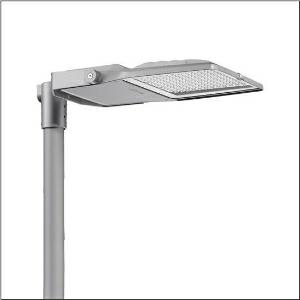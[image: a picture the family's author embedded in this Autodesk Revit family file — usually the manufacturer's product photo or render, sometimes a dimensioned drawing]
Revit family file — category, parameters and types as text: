
# Revit family: floodlight_fl_21_midi___pl64_5xa7782e2e3a_2f92
name_source: partatom
category: Lighting Fixtures
units: mm (PartAtom-declared; Revit-internal decimal feet)

## family parameters
Cut with Voids When Loaded = No
Host = Face
Light Source = No
Part Type = Normal
Room Calculation Point = No
Round Connector Dimension = Use Diameter
Shared = No

## types (1)
- --- (1 x LED, 25930 lm, 208.1 W, 3000K)
    Apparent Load = 208 VA
    CIE Flux Codes = 28 80 98 100 100
    Color Rendering = 70
    Color Temperature = 3000K
    Default Elevation = 1800 mm
    Description = Floodlight FL 21 midi, floodlight, primary light control with lens, of PMMA, primary optical cover: protective disc, of toughened safety glass, transparent, light distribution: PL64, light emission: direct distribution, installation type: surface-mounted, LED, High Power LED, rated luminous flux: 25.930lm, luminous efficacy: 124lm/W, light colour: 730, colour temperature: 3000K, control gear: ECG iQ, control: optimised constant luminous flux control (CLO 2.0), Desk-Remote (wireless, voltage-free reading and setting of iQ features in the workshop via application-optimized NFC function/RFID function), Smart-Wire, Night-Set, Temp-Guard, Auto-Match, Street-Remote, with terminal, 6-pole, mains connection: 220..240V, AC, 50/60Hz, start of lifetime: 208W, end of lifetime: 227W, reduction: 90W, luminaire housing, of diecast aluminium, powder-coated, Siteco® metallic grey (DB 702S), corrosivity category C5 according to DIN EN ISO 12944, mast bracket, of steel, galvanised, powder-coated, Siteco® metallic grey (DB 702S), protection rating (complete): IP66, insulation class (complete): insulation class II (safety insulation), certification: CE, protection symbol: D, impact resistance: IK08, permissible operating ambient temperature: -40..+40°C, permissible operating ambient temperature for outdoor applications: -40..+50°C, standard: DIN EN 12944, packaging unit: 1 piece

Light Distribution: PL64
    Height = 76 mm
    Lamp = 1 x LED
    Lamp Light Flux = 25930 lm
    Lamp Power = 208.1 W
    Lamp count = 1
    Length = 657 mm
    Luminous efficacy = 125 lm/W
    Manufacturer = Siteco
    ModVariant = No
    Model = 5XA7782E2E3A
    Number of Poles = 1
    OnlyDefault = Yes
    Power Factor = 1
    Product Name = Floodlight FL 21 midi | PL64
    Product group = floodlight | pylon top
    ProductGroupID = 6101
    Protection Class = Protection class II
    Protection Degree = IP 66
    RLX_Detail_Level = 1
    RlxData = <blob elided: 153205 chars, md5=48d80932>
    Socket = socket
    Standby Power = 0 W
    System Light Flux = 25930 lm
    System Power = 208 W
    Type Comments = factory setting: luminous flux: 100 % | dim-lin: 254 | 710 mA
    Type Image = l_1007123.jpg
    URL = http://relux.com
    VarID = @adj_015575
    Voltage = 0 V
    Weight = 0.00 kg
    Width = 442 mm

## geometry (parser evidence)
native form markers: Blend x4, Sweep x13
no freeform markers — native parametric forms only
